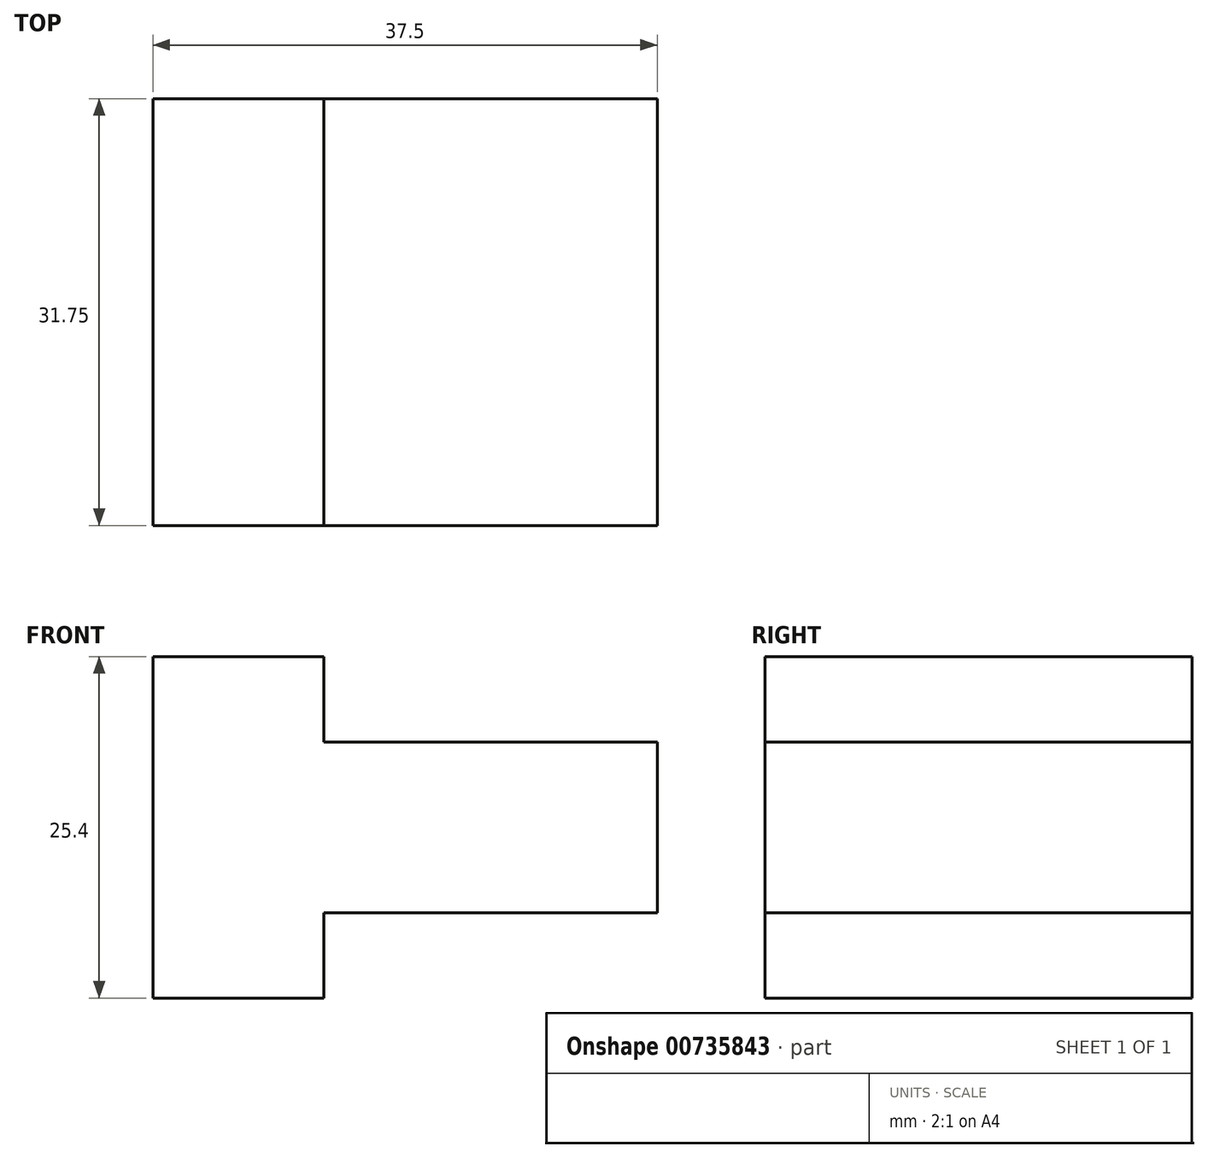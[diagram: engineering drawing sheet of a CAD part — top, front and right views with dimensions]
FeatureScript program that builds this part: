
annotation { "Feature Type Name" : "Feature", "Feature Type Description" : "" }
export const myFeature = defineFeature(function(context is Context, id is Id, definition is map)
    precondition{}
    {
        {
            var Q0;
            Q0=qCreatedBy(makeId("Front.planeOp"),FACE);
            var sketch = newSketch(context, id + "F0", { "sketchPlane" : qUnion([Q0])});
            skLineSegment(sketch, "E0", {"start": v(0, 0) * mm, "end": v(0, 25.4) * mm});
            skLineSegment(sketch, "E1", {"start": v(0, 25.4) * mm, "end": v(12.7, 25.4) * mm});
            skLineSegment(sketch, "E2", {"start": v(12.7, 25.4) * mm, "end": v(12.7, 19.05) * mm});
            skLineSegment(sketch, "E3", {"start": v(12.7, 19.05) * mm, "end": v(37.5, 19.05) * mm});
            skLineSegment(sketch, "E4", {"start": v(37.5, 19.05) * mm, "end": v(37.5, 6.35) * mm});
            skLineSegment(sketch, "E5", {"start": v(37.5, 6.35) * mm, "end": v(12.7, 6.35) * mm});
            skLineSegment(sketch, "E6", {"start": v(12.7, 6.35) * mm, "end": v(12.7, 0) * mm});
            skLineSegment(sketch, "E7", {"start": v(12.7, 0) * mm, "end": v(0, 0) * mm});
            skSolve(sketch);
        }
        {
            var Q0;
            Q0=makeQuery(id+"F0.imprint","IMPRINT",FACE,{"disambiguationData":[TD([[makeQuery(id+"F0.imprint","IMPRINT",EDGE,{"derivedFrom":sQuery(id+"F0.wireOp",EDGE,"E0")}),-1.0]])]});
            extrude(context, id + "F1", {"entities" : qUnion([Q0]), "depth" : 31.75 * mm, "offsetDistance" : 25.4 * mm});
        }
    });
